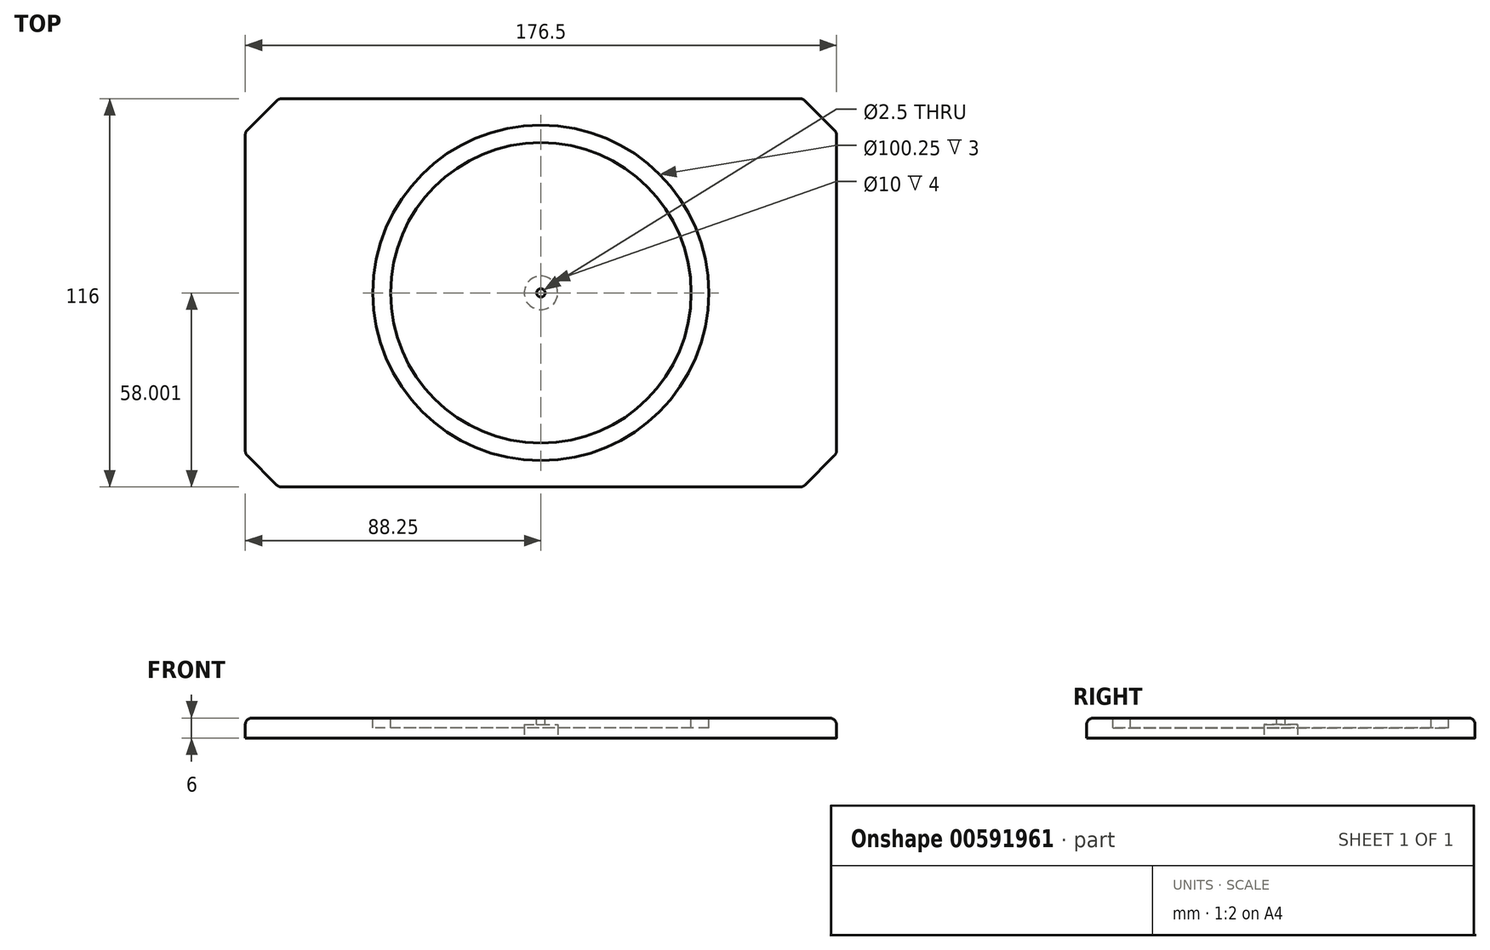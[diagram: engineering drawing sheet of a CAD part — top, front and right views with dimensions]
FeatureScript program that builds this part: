
annotation { "Feature Type Name" : "Feature", "Feature Type Description" : "" }
export const myFeature = defineFeature(function(context is Context, id is Id, definition is map)
    precondition{}
    {
        {
            var Q0;
            Q0=qCreatedBy(makeId("Top.planeOp"),FACE);
            var sketch = newSketch(context, id + "F0", { "sketchPlane" : qUnion([Q0])});
            skLineSegment(sketch, "E0.bottom", {"start": v(-91.65, 87.76) * mm, "end": v(84.85, 87.76) * mm});
            skLineSegment(sketch, "E0.top", {"start": v(-91.65, -28.24) * mm, "end": v(84.85, -28.24) * mm});
            skLineSegment(sketch, "E0.left", {"start": v(-91.65, 87.76) * mm, "end": v(-91.65, -28.24) * mm});
            skLineSegment(sketch, "E0.right", {"start": v(84.85, 87.76) * mm, "end": v(84.85, -28.24) * mm});
            skPoint(sketch, "E1", {"position": v(-3.4, -28.24) * mm});
            skPoint(sketch, "E2", {"position": v(84.85, 29.76) * mm});
            skSolve(sketch);
        }
        {
            var Q0;
            Q0=makeQuery(id+"F0.imprint","IMPRINT",FACE,{"disambiguationData":[TD([[makeQuery(id+"F0.imprint","IMPRINT",EDGE,{"derivedFrom":sQuery(id+"F0.wireOp",EDGE,"E0.bottom")}),-1.0]])]});
            extrude(context, id + "F1", {"entities" : qUnion([Q0]), "depth" : 6 * mm, "offsetDistance" : 25 * mm});
        }
        {
            var Q0;
            Q0=makeQuery(id+"F1.opExtrude","SWEPT_EDGE",EDGE,{"disambiguationData":[OSD([sQuery(id+"F0.wireOp",EDGE,"E0.top"),sQuery(id+"F0.wireOp",EDGE,"E0.left")])]});
            var Q1;
            Q1=makeQuery(id+"F1.opExtrude","SWEPT_EDGE",EDGE,{"disambiguationData":[OSD([sQuery(id+"F0.wireOp",EDGE,"E0.top"),sQuery(id+"F0.wireOp",EDGE,"E0.right")])]});
            var Q2;
            Q2=makeQuery(id+"F1.opExtrude","SWEPT_EDGE",EDGE,{"disambiguationData":[OSD([sQuery(id+"F0.wireOp",EDGE,"E0.bottom"),sQuery(id+"F0.wireOp",EDGE,"E0.right")])]});
            var Q3;
            Q3=makeQuery(id+"F1.opExtrude","SWEPT_EDGE",EDGE,{"disambiguationData":[OSD([sQuery(id+"F0.wireOp",EDGE,"E0.bottom"),sQuery(id+"F0.wireOp",EDGE,"E0.left")])]});
            chamfer(context, id + "F2", {"entities" : qUnion([Q0, Q1, Q2, Q3]), "width" : 10 * mm, "tangentPropagation" : true});
        }
        {
            var Q0;
            Q0=makeQuery(id+"F1.opExtrude","CAP_FACE",FACE,{"disambiguationData":[OSD([sQuery(id+"F0.wireOp",EDGE,"E0.bottom"),sQuery(id+"F0.wireOp",EDGE,"E0.top"),sQuery(id+"F0.wireOp",EDGE,"E0.left"),sQuery(id+"F0.wireOp",EDGE,"E0.right")])],"isStart":false});
            var sketch = newSketch(context, id + "F3", { "sketchPlane" : qUnion([Q0])});
            skLineSegment(sketch, "E3", {"start": v(-91.65, 29.76) * mm, "end": v(84.85, 29.76) * mm, "construction": true});
            skLineSegment(sketch, "E4", {"start": v(-3.4, 87.76) * mm, "end": v(-3.4, -28.24) * mm, "construction": true});
            skCircle(sketch, "E5", {"center": v(-3.4, 29.76) * mm, "radius": 50.12 * mm});
            skCircle(sketch, "E6", {"center": v(-3.4, 29.76) * mm, "radius": 44.88 * mm});
            skCircle(sketch, "E7", {"center": v(-3.4, 29.76) * mm, "radius": 1.25 * mm});
            skSolve(sketch);
        }
        {
            var Q0;
            Q0=makeQuery(id+"F1.opExtrude","CAP_EDGE",EDGE,{"disambiguationData":[OSD([sQuery(id+"F0.wireOp",EDGE,"E0.top")])],"isStart":false});
            var Q1;
            {var subQ0=sQuery(id+"F0.wireOp",EDGE,"E0.left");var subQ1=sQuery(id+"F0.wireOp",EDGE,"E0.top");Q1=makeQuery(id+"F2.opChamfer","BLEND_EDGE",EDGE,{"blendedFrom":[makeQuery(id+"F1.opExtrude","SWEPT_EDGE",EDGE,{"disambiguationData":[OSD([subQ1,subQ0])]}),makeQuery(id+"F1.opExtrude","CAP_FACE",FACE,{"disambiguationData":[OSD([sQuery(id+"F0.wireOp",EDGE,"E0.bottom"),subQ1,subQ0,sQuery(id+"F0.wireOp",EDGE,"E0.right")])],"isStart":false})],"blendedInto":[makeQuery(id+"F1.opExtrude","CAP_FACE",FACE,{"disambiguationData":[OSD([sQuery(id+"F0.wireOp",EDGE,"E0.bottom"),subQ1,subQ0,sQuery(id+"F0.wireOp",EDGE,"E0.right")])],"isStart":false})]});}
            var Q2;
            Q2=makeQuery(id+"F1.opExtrude","CAP_EDGE",EDGE,{"disambiguationData":[OSD([sQuery(id+"F0.wireOp",EDGE,"E0.left")])],"isStart":false});
            var Q3;
            {var subQ0=sQuery(id+"F0.wireOp",EDGE,"E0.left");var subQ1=sQuery(id+"F0.wireOp",EDGE,"E0.bottom");Q3=makeQuery(id+"F2.opChamfer","BLEND_EDGE",EDGE,{"blendedFrom":[makeQuery(id+"F1.opExtrude","SWEPT_EDGE",EDGE,{"disambiguationData":[OSD([subQ1,subQ0])]}),makeQuery(id+"F1.opExtrude","CAP_FACE",FACE,{"disambiguationData":[OSD([subQ1,sQuery(id+"F0.wireOp",EDGE,"E0.top"),subQ0,sQuery(id+"F0.wireOp",EDGE,"E0.right")])],"isStart":false})],"blendedInto":[makeQuery(id+"F1.opExtrude","CAP_FACE",FACE,{"disambiguationData":[OSD([subQ1,sQuery(id+"F0.wireOp",EDGE,"E0.top"),subQ0,sQuery(id+"F0.wireOp",EDGE,"E0.right")])],"isStart":false})]});}
            var Q4;
            Q4=makeQuery(id+"F1.opExtrude","CAP_EDGE",EDGE,{"disambiguationData":[OSD([sQuery(id+"F0.wireOp",EDGE,"E0.bottom")])],"isStart":false});
            var Q5;
            {var subQ0=sQuery(id+"F0.wireOp",EDGE,"E0.right");var subQ1=sQuery(id+"F0.wireOp",EDGE,"E0.bottom");Q5=makeQuery(id+"F2.opChamfer","BLEND_EDGE",EDGE,{"blendedFrom":[makeQuery(id+"F1.opExtrude","SWEPT_EDGE",EDGE,{"disambiguationData":[OSD([subQ1,subQ0])]}),makeQuery(id+"F1.opExtrude","CAP_FACE",FACE,{"disambiguationData":[OSD([subQ1,sQuery(id+"F0.wireOp",EDGE,"E0.top"),sQuery(id+"F0.wireOp",EDGE,"E0.left"),subQ0])],"isStart":false})],"blendedInto":[makeQuery(id+"F1.opExtrude","CAP_FACE",FACE,{"disambiguationData":[OSD([subQ1,sQuery(id+"F0.wireOp",EDGE,"E0.top"),sQuery(id+"F0.wireOp",EDGE,"E0.left"),subQ0])],"isStart":false})]});}
            var Q6;
            Q6=makeQuery(id+"F1.opExtrude","CAP_EDGE",EDGE,{"disambiguationData":[OSD([sQuery(id+"F0.wireOp",EDGE,"E0.right")])],"isStart":false});
            var Q7;
            {var subQ0=sQuery(id+"F0.wireOp",EDGE,"E0.right");var subQ1=sQuery(id+"F0.wireOp",EDGE,"E0.top");Q7=makeQuery(id+"F2.opChamfer","BLEND_EDGE",EDGE,{"blendedFrom":[makeQuery(id+"F1.opExtrude","SWEPT_EDGE",EDGE,{"disambiguationData":[OSD([subQ1,subQ0])]}),makeQuery(id+"F1.opExtrude","CAP_FACE",FACE,{"disambiguationData":[OSD([sQuery(id+"F0.wireOp",EDGE,"E0.bottom"),subQ1,sQuery(id+"F0.wireOp",EDGE,"E0.left"),subQ0])],"isStart":false})],"blendedInto":[makeQuery(id+"F1.opExtrude","CAP_FACE",FACE,{"disambiguationData":[OSD([sQuery(id+"F0.wireOp",EDGE,"E0.bottom"),subQ1,sQuery(id+"F0.wireOp",EDGE,"E0.left"),subQ0])],"isStart":false})]});}
            var Q8;
            {var subQ0=sQuery(id+"F0.wireOp",EDGE,"E0.top");Q8=makeQuery(id+"F2.opChamfer","BLEND_EDGE",EDGE,{"blendedFrom":[makeQuery(id+"F1.opExtrude","SWEPT_EDGE",EDGE,{"disambiguationData":[OSD([subQ0,sQuery(id+"F0.wireOp",EDGE,"E0.left")])]}),makeQuery(id+"F1.opExtrude","SWEPT_FACE",FACE,{"disambiguationData":[OSD([subQ0])]})],"blendedInto":[makeQuery(id+"F1.opExtrude","SWEPT_FACE",FACE,{"disambiguationData":[OSD([subQ0])]})]});}
            var Q9;
            {var subQ0=sQuery(id+"F0.wireOp",EDGE,"E0.left");Q9=makeQuery(id+"F2.opChamfer","BLEND_EDGE",EDGE,{"blendedFrom":[makeQuery(id+"F1.opExtrude","SWEPT_EDGE",EDGE,{"disambiguationData":[OSD([sQuery(id+"F0.wireOp",EDGE,"E0.top"),subQ0])]}),makeQuery(id+"F1.opExtrude","SWEPT_FACE",FACE,{"disambiguationData":[OSD([subQ0])]})],"blendedInto":[makeQuery(id+"F1.opExtrude","SWEPT_FACE",FACE,{"disambiguationData":[OSD([subQ0])]})]});}
            var Q10;
            {var subQ0=sQuery(id+"F0.wireOp",EDGE,"E0.left");Q10=makeQuery(id+"F2.opChamfer","BLEND_EDGE",EDGE,{"blendedFrom":[makeQuery(id+"F1.opExtrude","SWEPT_EDGE",EDGE,{"disambiguationData":[OSD([sQuery(id+"F0.wireOp",EDGE,"E0.bottom"),subQ0])]}),makeQuery(id+"F1.opExtrude","SWEPT_FACE",FACE,{"disambiguationData":[OSD([subQ0])]})],"blendedInto":[makeQuery(id+"F1.opExtrude","SWEPT_FACE",FACE,{"disambiguationData":[OSD([subQ0])]})]});}
            var Q11;
            {var subQ0=sQuery(id+"F0.wireOp",EDGE,"E0.bottom");Q11=makeQuery(id+"F2.opChamfer","BLEND_EDGE",EDGE,{"blendedFrom":[makeQuery(id+"F1.opExtrude","SWEPT_EDGE",EDGE,{"disambiguationData":[OSD([subQ0,sQuery(id+"F0.wireOp",EDGE,"E0.left")])]}),makeQuery(id+"F1.opExtrude","SWEPT_FACE",FACE,{"disambiguationData":[OSD([subQ0])]})],"blendedInto":[makeQuery(id+"F1.opExtrude","SWEPT_FACE",FACE,{"disambiguationData":[OSD([subQ0])]})]});}
            var Q12;
            {var subQ0=sQuery(id+"F0.wireOp",EDGE,"E0.bottom");Q12=makeQuery(id+"F2.opChamfer","BLEND_EDGE",EDGE,{"blendedFrom":[makeQuery(id+"F1.opExtrude","SWEPT_EDGE",EDGE,{"disambiguationData":[OSD([subQ0,sQuery(id+"F0.wireOp",EDGE,"E0.right")])]}),makeQuery(id+"F1.opExtrude","SWEPT_FACE",FACE,{"disambiguationData":[OSD([subQ0])]})],"blendedInto":[makeQuery(id+"F1.opExtrude","SWEPT_FACE",FACE,{"disambiguationData":[OSD([subQ0])]})]});}
            var Q13;
            {var subQ0=sQuery(id+"F0.wireOp",EDGE,"E0.right");Q13=makeQuery(id+"F2.opChamfer","BLEND_EDGE",EDGE,{"blendedFrom":[makeQuery(id+"F1.opExtrude","SWEPT_EDGE",EDGE,{"disambiguationData":[OSD([sQuery(id+"F0.wireOp",EDGE,"E0.bottom"),subQ0])]}),makeQuery(id+"F1.opExtrude","SWEPT_FACE",FACE,{"disambiguationData":[OSD([subQ0])]})],"blendedInto":[makeQuery(id+"F1.opExtrude","SWEPT_FACE",FACE,{"disambiguationData":[OSD([subQ0])]})]});}
            var Q14;
            {var subQ0=sQuery(id+"F0.wireOp",EDGE,"E0.right");Q14=makeQuery(id+"F2.opChamfer","BLEND_EDGE",EDGE,{"blendedFrom":[makeQuery(id+"F1.opExtrude","SWEPT_EDGE",EDGE,{"disambiguationData":[OSD([sQuery(id+"F0.wireOp",EDGE,"E0.top"),subQ0])]}),makeQuery(id+"F1.opExtrude","SWEPT_FACE",FACE,{"disambiguationData":[OSD([subQ0])]})],"blendedInto":[makeQuery(id+"F1.opExtrude","SWEPT_FACE",FACE,{"disambiguationData":[OSD([subQ0])]})]});}
            var Q15;
            {var subQ0=sQuery(id+"F0.wireOp",EDGE,"E0.top");Q15=makeQuery(id+"F2.opChamfer","BLEND_EDGE",EDGE,{"blendedFrom":[makeQuery(id+"F1.opExtrude","SWEPT_EDGE",EDGE,{"disambiguationData":[OSD([subQ0,sQuery(id+"F0.wireOp",EDGE,"E0.right")])]}),makeQuery(id+"F1.opExtrude","SWEPT_FACE",FACE,{"disambiguationData":[OSD([subQ0])]})],"blendedInto":[makeQuery(id+"F1.opExtrude","SWEPT_FACE",FACE,{"disambiguationData":[OSD([subQ0])]})]});}
            fillet(context, id + "F4", {"entities" : qUnion([Q0, Q1, Q2, Q3, Q4, Q5, Q6, Q7, Q8, Q9, Q10, Q11, Q12, Q13, Q14, Q15]), "radius" : 2 * mm, "tangentPropagation" : true, "allowEdgeOverflow" : false});
        }
        {
            var Q0;
            Q0=makeQuery(id+"F3.imprint","IMPRINT",FACE,{"disambiguationData":[TD([[makeQuery(id+"F3.imprint","IMPRINT",EDGE,{"derivedFrom":sQuery(id+"F3.wireOp",EDGE,"E5")}),1.0]])]});
            extrude(context, id + "F5", {"entities" : qUnion([Q0]), "operationType" : NewBodyOperationType.REMOVE, "oppositeDirection" : true, "depth" : 3 * mm, "offsetDistance" : 25 * mm});
        }
        {
            var Q0;
            Q0=makeQuery(id+"F3.imprint","IMPRINT",FACE,{"disambiguationData":[TD([[makeQuery(id+"F3.imprint","IMPRINT",EDGE,{"derivedFrom":sQuery(id+"F3.wireOp",EDGE,"E7")}),1.0]])]});
            extrude(context, id + "F6", {"entities" : qUnion([Q0]), "operationType" : NewBodyOperationType.REMOVE, "endBound" : BoundingType.THROUGH_ALL, "oppositeDirection" : true, "depth" : 25 * mm, "offsetDistance" : 25 * mm});
        }
        {
            var Q0;
            Q0=makeQuery(id+"F1.opExtrude","CAP_FACE",FACE,{"disambiguationData":[OSD([sQuery(id+"F0.wireOp",EDGE,"E0.bottom"),sQuery(id+"F0.wireOp",EDGE,"E0.top"),sQuery(id+"F0.wireOp",EDGE,"E0.left"),sQuery(id+"F0.wireOp",EDGE,"E0.right")])],"isStart":true});
            var sketch = newSketch(context, id + "F7", { "sketchPlane" : qUnion([Q0])});
            skCircle(sketch, "E8", {"center": v(-3.4, -29.76) * mm, "radius": 5 * mm});
            skSolve(sketch);
        }
        {
            var Q0;
            Q0 = qSketchRegion(id + "F7", true);
            extrude(context, id + "F8", {"entities" : qUnion([Q0]), "operationType" : NewBodyOperationType.REMOVE, "oppositeDirection" : true, "depth" : 4 * mm, "offsetDistance" : 25 * mm});
        }
    });
